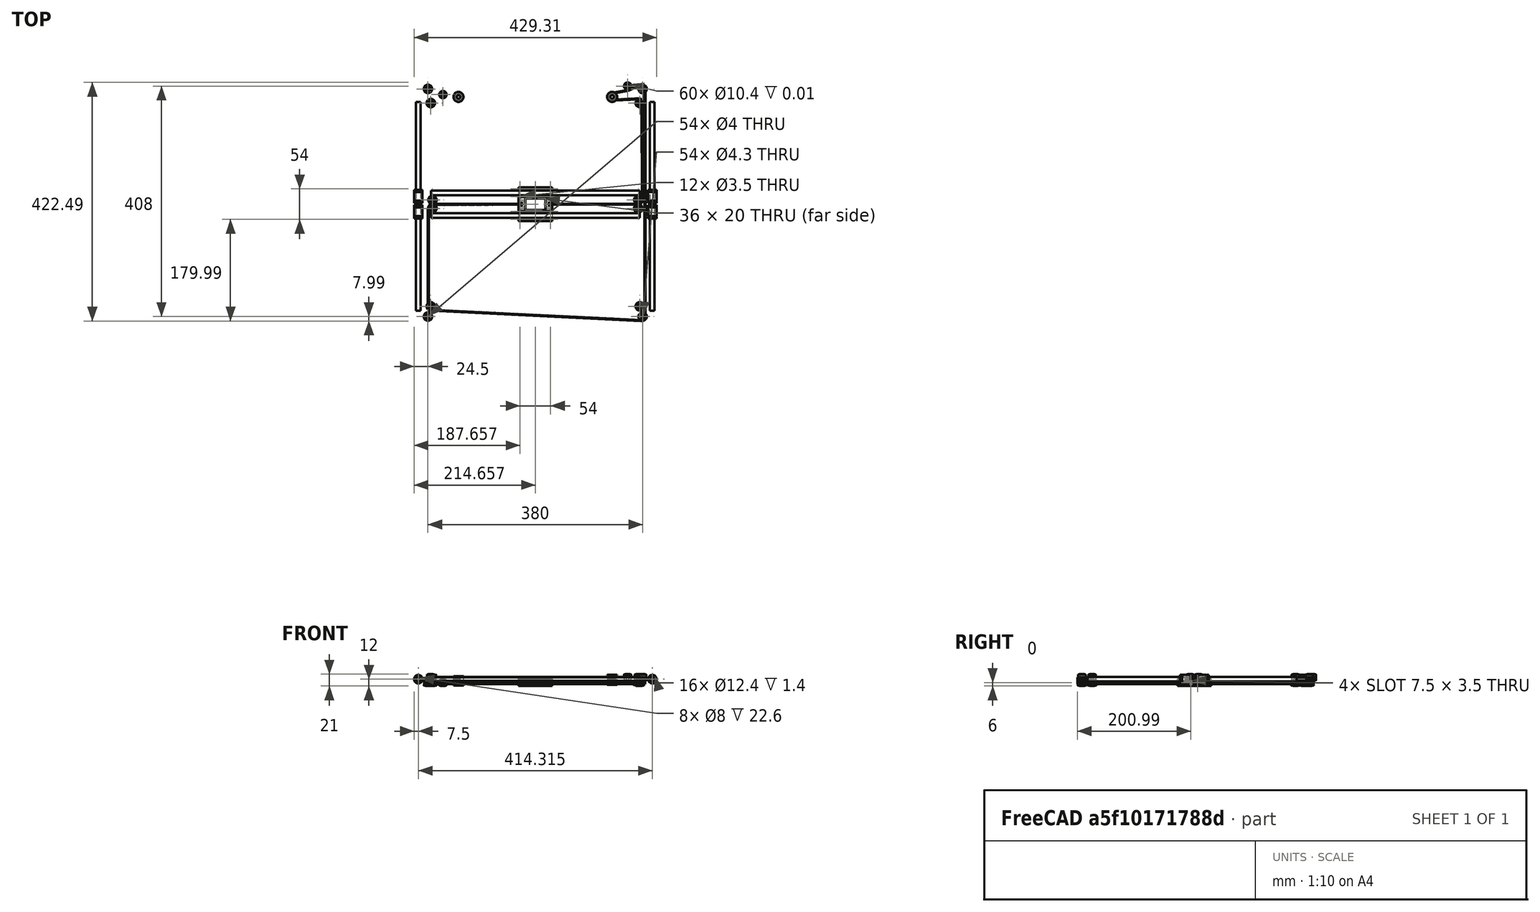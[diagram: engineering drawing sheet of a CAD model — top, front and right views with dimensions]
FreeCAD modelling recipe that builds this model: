
FCSTD DOCUMENT  (FreeCAD 0.16R4945 (Git))
Label: GT2-Belt_right
License: All rights reserved
LicenseURL: http://en.wikipedia.org/wiki/All_rights_reserved
objects: Part::Part2DObjectPython×17, Sketcher::SketchObject×5, Part::FeaturePython×3, App::DocumentObjectGroup×3, Part::Sweep×2, PartDesign::Pad×1, Part::Compound×1
note: 30 computed .brp shape members not serialized (recipe doc carries the construction recipe); baked Part::Feature solids carry a one-line shape summary decoded from their .brp

FEATURE [Part::FeaturePython] muxedAssembly  # WARN: FeaturePython — macro-defined, semantics opaque (R4)
  type = muxedAssembly
FEATURE [Sketcher::SketchObject] Sketch  label="Beltpath"
  ExternalGeometry = -> [muxedAssembly]
  Placement = pos=(0,0,13.243) rot=(0,0,1;0rad)
  Support = -> muxedAssembly [Face372]
  sketch-geometry (26):
    g0: LineSegment [constr] StartX=190.157 StartY=-169 StartZ=0 EndX=250.157 EndY=-169 EndZ=0
    g1: Circle [constr] CenterX=38 CenterY=-176.5 CenterZ=0 NormalX=0 NormalY=0 NormalZ=1 Radius=7.25
    g2: Circle [constr] CenterX=38 CenterY=-350 CenterZ=0 NormalX=0 NormalY=0 NormalZ=1 Radius=7.25
    g3: Circle [constr] CenterX=407 CenterY=-368 CenterZ=0 NormalX=0 NormalY=0 NormalZ=1 Radius=7.25
    g4: Circle [constr] CenterX=402.315 CenterY=-161.5 CenterZ=0 NormalX=0 NormalY=0 NormalZ=1 Radius=7.25
    g5: Circle [constr] CenterX=407 CenterY=35 CenterZ=0 NormalX=0 NormalY=0 NormalZ=1 Radius=7.25
    g6: Circle [constr] CenterX=402 CenterY=10 CenterZ=0 NormalX=0 NormalY=0 NormalZ=1 Radius=7.25
    g7: Circle [constr] CenterX=356 CenterY=21 CenterZ=0 NormalX=0 NormalY=0 NormalZ=1 Radius=6.04449
    g8: LineSegment StartX=250.157 StartY=-169 StartZ=0 EndX=402.327 EndY=-168.75 EndZ=0
    g9: ArcOfCircle CenterX=402.315 CenterY=-161.5 CenterZ=0 NormalX=0 NormalY=0 NormalZ=1 Radius=7.25 StartAngle=4.71403 EndAngle=6.28502
    g10: LineSegment StartX=409.565 StartY=-161.487 StartZ=0 EndX=409.25 EndY=10.0133 EndZ=0
    g11: ArcOfCircle CenterX=402 CenterY=10 CenterZ=0 NormalX=0 NormalY=0 NormalZ=1 Radius=7.25 StartAngle=0.00183673 EndAngle=1.621
    g12: LineSegment StartX=401.636 StartY=17.2409 StartZ=0 EndX=356.303 EndY=14.9631 EndZ=0
    g13: ArcOfCircle CenterX=356 CenterY=21 CenterZ=0 NormalX=0 NormalY=0 NormalZ=1 Radius=6.04449 StartAngle=1.76381 EndAngle=4.76259
    g14: ArcOfCircle CenterX=407 CenterY=35 CenterZ=0 NormalX=0 NormalY=0 NormalZ=1 Radius=7.26076 StartAngle=6.28316 EndAngle=8.24177
    g15: LineSegment StartX=414.261 StartY=34.9998 StartZ=0 EndX=414.25 EndY=-368 EndZ=0
    g16: ArcOfCircle CenterX=407 CenterY=-368 CenterZ=0 NormalX=0 NormalY=0 NormalZ=1 Radius=7.25 StartAngle=4.66365 EndAngle=6.28316
    g17: LineSegment StartX=406.647 StartY=-375.241 StartZ=0 EndX=37.6468 EndY=-357.241 EndZ=0
    g18: ArcOfCircle CenterX=38 CenterY=-350 CenterZ=0 NormalX=0 NormalY=0 NormalZ=1 Radius=7.25 StartAngle=3.14159 EndAngle=4.66365
    g19: LineSegment StartX=30.75 StartY=-350 StartZ=0 EndX=30.75 EndY=-176.5 EndZ=0
    g20: ArcOfCircle CenterX=38 CenterY=-176.5 CenterZ=0 NormalX=0 NormalY=0 NormalZ=1 Radius=7.25 StartAngle=1.57244 EndAngle=3.14159
    g21: LineSegment StartX=37.9881 StartY=-169.25 StartZ=0 EndX=190.157 EndY=-169 EndZ=0
    g22: Circle [constr] CenterX=383.517 CenterY=39.9241 CenterZ=0 NormalX=0 NormalY=0 NormalZ=1 Radius=7.25
    g23: LineSegment StartX=404.254 StartY=41.7216 StartZ=0 EndX=386.62 EndY=33.3716 EndZ=0
    g24: ArcOfCircle CenterX=383.517 CenterY=39.9241 CenterZ=0 NormalX=0 NormalY=0 NormalZ=1 Radius=7.25 StartAngle=4.9054 EndAngle=5.15462
    g25: LineSegment StartX=384.908 StartY=32.8088 StartZ=0 EndX=354.841 EndY=26.9323 EndZ=0
  constraints (67):
    c: PointOnObject(g0,g-6)
    c: PointOnObject(g0,g-7)
    c: Symmetric(g-6,g-6,g0)
    c: Coincident(g1,g-5)
    c: Coincident(g4,g-4)
    c: Coincident(g7,g-3)
    c: Radius(g7) = 6.04449
    c: Radius(g5) = 7.25
    c: Equal(g5,g6)
    c: Equal(g6,g4)
    c: Equal(g4,g1)
    c: Equal(g1,g2)
    c: Equal(g2,g3)
    c: Coincident(g0,g8)
    c: Tangent(g8,g9) = -1.5708
    c: Coincident(g9,g10)
    c: Tangent(g10,g11) = -1.5708
    c: Coincident(g11,g12)
    c: Tangent(g12,g13) = 1.5708
    c: Coincident(g14,g15)
    c: Tangent(g15,g16) = 1.5708
    c: Coincident(g16,g17)
    c: Tangent(g17,g18) = 1.5708
    c: Coincident(g18,g19)
    c: Tangent(g19,g20) = 1.5708
    c: Coincident(g20,g21)
    c: Coincident(g21,g0)
    c: Coincident(g4,g9)
    c: Coincident(g6,g11)
    c: Coincident(g7,g13)
    c: Coincident(g5,g14)
    c: Coincident(g3,g16)
    c: Coincident(g18,g2)
    c: Coincident(g1,g20)
    c: PointOnObject(g8,g4)
    c: Tangent(g9,g10) = -1.5708
    c: PointOnObject(g10,g6)
    c: Tangent(g11,g12) = -1.5708
    c: PointOnObject(g12,g7)
    c: Tangent(g14,g15) = 1.5708
    c: PointOnObject(g15,g3)
    c: Tangent(g16,g17) = 1.5708
    c: PointOnObject(g17,g2)
    c: Tangent(g18,g19) = 1.5708
    c: PointOnObject(g19,g1)
    c: Tangent(g20,g21) = 1.5708
    c: Equal(g22,g5)
    c: Coincident(g14,g23)
    c: Tangent(g23,g5)
    c: Tangent(g23,g24) = 1.5708
    c: Coincident(g24,g25)
    c: Coincident(g25,g13)
    c: Tangent(g25,g7)
    c: PointOnObject(g23,g22)
    c: DistanceX(g22) = 383.517
    c: DistanceY(g22) = 39.9241
    c: PointOnObject(g24,g22)
    c: Tangent(g24,g25) = 1.5708
    c: Coincident(g22,g24)
    c: DistanceY(g-11,g2) = 0
    c: DistanceX(g-11,g2) = 3
    c: DistanceY(g3,g-10) = 0
    c: DistanceX(g-10,g3) = -3
    c: DistanceY(g6,g-8) = 0
    c: DistanceX(g6,g-8) = 3
    c: DistanceY(g5,g-9) = 0
    c: DistanceX(g5,g-9) = 3
FEATURE [Sketcher::SketchObject] Sketch001
  Placement = pos=(250.157,0,0) rot=(0.57735,0.57735,0.57735;2.0944rad)
  Support = -> muxedAssembly [Face737]
  sketch-geometry (4):
    g0: LineSegment StartX=-169.757 StartY=13.2439 StartZ=0 EndX=-168.257 EndY=13.2439 EndZ=0
    g1: LineSegment StartX=-168.257 StartY=13.2439 StartZ=0 EndX=-168.257 EndY=19.2439 EndZ=0
    g2: LineSegment StartX=-168.257 StartY=19.2439 StartZ=0 EndX=-169.757 EndY=19.2439 EndZ=0
    g3: LineSegment StartX=-169.757 StartY=19.2439 StartZ=0 EndX=-169.757 EndY=13.2439 EndZ=0
  constraints (10):
    c: Coincident(g0,g1)
    c: Coincident(g1,g2)
    c: Coincident(g2,g3)
    c: Coincident(g3,g0)
    c: Horizontal(g0)
    c: Horizontal(g2)
    c: Vertical(g1)
    c: Vertical(g3)
    c: Distance(g2) = 1.5
    c: Distance(g1) = 6
FEATURE [Part::FeaturePython] Bearings_import01  # a2plus imported part (geometry in sourceFile) (typed FeaturePython)
  fixedPosition = true
  sourceFile = <userpath>/CloudStation/Hobbyprojekte/3D Drucker/CoreXY/Freecad/Assembly/XY/Bearings.FCStd
  timeLastImport = 1431280628
FEATURE [Part::Sweep] Sweep  label="Sweep (GT2-Belt simple)"
  Frenet = false
  Sections = -> [Sketch001]
  Solid = true
  Spine = -> Sketch [Edge1,Edge2,Edge3,Edge4,Edge5,Edge6,Edge7,Edge8,Edge9,Edge10,Edge11,Edge12,Edge13,Edge14,Edge15,Edge16,Edge17]
  Transition = 1
FEATURE [Sketcher::SketchObject] Sketch002  label="Timing Belt Master Sketch"
  Placement = pos=(0,0,0) rot=(1,0,0;1.5708rad)
  sketch-geometry (11):
    g0: Circle CenterX=0 CenterY=-0.449 CenterZ=0 NormalX=0 NormalY=0 NormalZ=1 Radius=0.555
    g1: LineSegment [constr] StartX=-1 StartY=-1.004 StartZ=0 EndX=1 EndY=-1.004 EndZ=0
    g2: LineSegment StartX=-1 StartY=-0.254 StartZ=0 EndX=1 EndY=-0.254 EndZ=0
    g3: LineSegment StartX=-1 StartY=0.376 StartZ=0 EndX=1 EndY=0.376 EndZ=0
    g4: LineSegment StartX=-1 StartY=0.376 StartZ=0 EndX=-1 EndY=-1.004 EndZ=0
    g5: LineSegment StartX=1 StartY=0.376 StartZ=0 EndX=1 EndY=-1.004 EndZ=0
    g6: LineSegment [constr] StartX=-1 StartY=-0.449 StartZ=0 EndX=1 EndY=-0.449 EndZ=0
    g7: Circle CenterX=-0.740175 CenterY=-0.404 CenterZ=0 NormalX=0 NormalY=0 NormalZ=1 Radius=0.15
    g8: Circle CenterX=0.740175 CenterY=-0.404 CenterZ=0 NormalX=0 NormalY=0 NormalZ=1 Radius=0.15
    g9: Circle CenterX=-0.4 CenterY=-0.254 CenterZ=0 NormalX=0 NormalY=0 NormalZ=1 Radius=1
    g10: Circle CenterX=0.4 CenterY=-0.254 CenterZ=0 NormalX=0 NormalY=0 NormalZ=1 Radius=1
  constraints (33):
    c: Radius(g0) = 0.555
    c: PointOnObject(g0,g-2)
    c: Horizontal(g1)
    c: Tangent(g1,g0)
    c: DistanceX(g1) = 2
    c: Symmetric(g1,g1,g-2)
    c: Horizontal(g2)
    c: DistanceY(g2,g1) = -0.75
    c: Horizontal(g3)
    c: Equal(g1,g2)
    c: Equal(g2,g3)
    c: Vertical(g4)
    c: Coincident(g4,g1)
    c: Coincident(g4,g3)
    c: PointOnObject(g2,g4)
    c: Coincident(g5,g1)
    c: Coincident(g5,g3)
    c: DistanceY(g3,g1) = -1.38
    c: PointOnObject(g0,g6)
    c: DistanceY(g-1,g2) = -0.254
    c: Horizontal(g6)
    c: PointOnObject(g6,g4)
    c: PointOnObject(g6,g5)
    c: Radius(g7) = 0.15
    c: Equal(g8,g7)
    c: Symmetric(g7,g8,g-2)
    c: Radius(g9) = 1
    c: Equal(g10,g9)
    c: Symmetric(g10,g9,g-2)
    c: DistanceX(g-1,g10) = 0.4
    c: DistanceY(g7,g3) = 0.78
    c: DistanceX(g7,g3) = -0.259825
    c: PointOnObject(g10,g2)
FEATURE [App::DocumentObjectGroup] Group  label="Master Sketch"
  Group = -> [Sketch002]
FEATURE [Part::Part2DObjectPython] Circle  # Draft 2D object (typed FeaturePython)
  FirstAngle = 0
  LastAngle = 0
  MakeFace = true
  Placement = pos=(0,-0.449,0) rot=(0,0,1;0rad)
  Radius = 0.555
FEATURE [Part::Part2DObjectPython] Line  # Draft 2D object (typed FeaturePython)
  ChamferSize = 0
  Closed = false
  End = (1,-0.254,0)
  FilletRadius = 0
  MakeFace = true
  Points = (2) [(-1,-0.254,0),(1,-0.254,0)]
  Start = (-1,-0.254,0)
FEATURE [Part::Part2DObjectPython] DWire  # Draft 2D object (typed FeaturePython)
  ChamferSize = 0
  Closed = false
  End = (1,-1.004,0)
  FilletRadius = 0
  MakeFace = true
  Points = (4) [(-1,-1.004,0),(-1,0.376,0),(1,0.376,0),(1,-1.004,0)]
  Start = (-1,-1.004,0)
FEATURE [Part::Part2DObjectPython] Circle001  # Draft 2D object (typed FeaturePython)
  FirstAngle = 0
  LastAngle = 0
  MakeFace = true
  Placement = pos=(-0.740175,-0.404,0) rot=(0,0,1;0rad)
  Radius = 0.15
FEATURE [Part::Part2DObjectPython] Circle002  # Draft 2D object (typed FeaturePython)
  FirstAngle = 0
  LastAngle = 0
  MakeFace = true
  Placement = pos=(0.740175,-0.404,0) rot=(0,0,1;0rad)
  Radius = 0.15
FEATURE [Part::Part2DObjectPython] Circle003  # Draft 2D object (typed FeaturePython)
  FirstAngle = 0
  LastAngle = 0
  MakeFace = true
  Placement = pos=(-0.4,-0.254,0) rot=(0,0,1;0rad)
  Radius = 1
FEATURE [Part::Part2DObjectPython] Circle004  # Draft 2D object (typed FeaturePython)
  FirstAngle = 0
  LastAngle = 0
  MakeFace = true
  Placement = pos=(0.4,-0.254,0) rot=(0,0,1;0rad)
  Radius = 1
FEATURE [App::DocumentObjectGroup] Group001  label="Draft from Sketch"
  Group = -> [Circle,Line,DWire,Circle001,Circle002,Circle003,Circle004]
FEATURE [Part::Part2DObjectPython] Arc  # Draft 2D object (typed FeaturePython)
  FirstAngle = 7.49472
  LastAngle = 90
  MakeFace = false
  Placement = pos=(-0.740175,-0.404,0) rot=(0,0,1;0rad)
  Radius = 0.15
FEATURE [Part::Part2DObjectPython] Arc001  # Draft 2D object (typed FeaturePython)
  FirstAngle = 90
  LastAngle = 172.505
  MakeFace = false
  Placement = pos=(0.740175,-0.404,0) rot=(0,0,1;0rad)
  Radius = 0.15
FEATURE [Part::Part2DObjectPython] Line001  # Draft 2D object (typed FeaturePython)
  ChamferSize = 0
  Closed = false
  End = (-1,-0.254,0)
  FilletRadius = 0
  MakeFace = false
  Points = (2) [(-0.740175,-0.254,0),(-1,-0.254,0)]
  Start = (-0.740175,-0.254,0)
FEATURE [Part::Part2DObjectPython] Line002  # Draft 2D object (typed FeaturePython)
  ChamferSize = 0
  Closed = false
  End = (1,-0.254,0)
  FilletRadius = 0
  MakeFace = false
  Points = (2) [(0.740175,-0.254,0),(1,-0.254,0)]
  Start = (0.740175,-0.254,0)
FEATURE [Part::Part2DObjectPython] Arc002  # Draft 2D object (typed FeaturePython)
  FirstAngle = -154.011
  LastAngle = -25.9892
  MakeFace = false
  Placement = pos=(0,-0.449,0) rot=(0,0,1;0rad)
  Radius = 0.555
FEATURE [Part::Part2DObjectPython] Arc003  # Draft 2D object (typed FeaturePython)
  FirstAngle = -25.9892
  LastAngle = -7.49472
  MakeFace = false
  Placement = pos=(-0.4,-0.254,0) rot=(0,0,1;0rad)
  Radius = 1
FEATURE [Part::Part2DObjectPython] Arc004  # Draft 2D object (typed FeaturePython)
  FirstAngle = -172.505
  LastAngle = -154.011
  MakeFace = false
  Placement = pos=(0.4,-0.254,0) rot=(0,0,1;0rad)
  Radius = 1
FEATURE [Part::Part2DObjectPython] Line003  # Draft 2D object (typed FeaturePython)
  ChamferSize = 0
  Closed = false
  End = (-1,0.376,0)
  FilletRadius = 0
  MakeFace = false
  Points = (2) [(-1,-0.254,0),(-1,0.376,0)]
  Start = (-1,-0.254,0)
FEATURE [Part::Part2DObjectPython] Line004  # Draft 2D object (typed FeaturePython)
  ChamferSize = 0
  Closed = false
  End = (1,0.376,0)
  FilletRadius = 0
  MakeFace = false
  Points = (2) [(1,-0.254,0),(1,0.376,0)]
  Start = (1,-0.254,0)
FEATURE [Part::Part2DObjectPython] Line005  # Draft 2D object (typed FeaturePython)
  ChamferSize = 0
  Closed = false
  End = (1,0.376,0)
  FilletRadius = 0
  MakeFace = false
  Points = (2) [(-1,0.376,0),(1,0.376,0)]
  Start = (-1,0.376,0)
FEATURE [App::DocumentObjectGroup] Group002  label="Outline from Draft"
  Group = -> [Arc,Arc001,Line001,Line002,Arc002,Arc003,Arc004,Line003,Line004,Line005]
FEATURE [Sketcher::SketchObject] Sketch003  label="Timing Belt sketch from outline"
  Placement = pos=(0,0,0) rot=(0,-0.707107,0.707107;3.14159rad)
  sketch-geometry (10):
    g0: ArcOfCircle CenterX=-0.740173 CenterY=-0.403997 CenterZ=0 NormalX=0 NormalY=0 NormalZ=1 Radius=0.149997 StartAngle=0.134719 EndAngle=1.57082
    g1: LineSegment StartX=1 StartY=-0.254 StartZ=0 EndX=1 EndY=0.376 EndZ=0
    g2: ArcOfCircle CenterX=0.740176 CenterY=-0.404 CenterZ=0 NormalX=0 NormalY=0 NormalZ=1 Radius=0.15 StartAngle=1.5708 EndAngle=3.01411
    g3: LineSegment StartX=0.740176 StartY=-0.254 StartZ=0 EndX=1 EndY=-0.254 EndZ=0
    g4: LineSegment StartX=-0.740176 StartY=-0.254 StartZ=0 EndX=-1 EndY=-0.254 EndZ=0
    g5: ArcOfCircle CenterX=0 CenterY=-0.448894 CenterZ=0 NormalX=0 NormalY=0 NormalZ=1 Radius=0.555048 StartAngle=3.59519 EndAngle=5.83002
    g6: ArcOfCircle CenterX=-0.400001 CenterY=-0.254 CenterZ=0 NormalX=0 NormalY=0 NormalZ=1 Radius=1 StartAngle=5.82992 EndAngle=6.15188
    g7: LineSegment StartX=-1 StartY=0.376 StartZ=0 EndX=1 EndY=0.376 EndZ=0
    g8: ArcOfCircle CenterX=0.400001 CenterY=-0.254 CenterZ=0 NormalX=0 NormalY=0 NormalZ=1 Radius=1 StartAngle=3.27181 EndAngle=3.5951
    g9: LineSegment StartX=-1 StartY=-0.254 StartZ=0 EndX=-1 EndY=0.376 EndZ=0
  constraints (34):
    c: Coincident(g7,g9)
    c: Coincident(g1,g7)
    c: Coincident(g4,g9)
    c: Coincident(g0,g4)
    c: Coincident(g0,g8)
    c: Coincident(g5,g8)
    c: Coincident(g5,g6)
    c: Coincident(g2,g6)
    c: Coincident(g2,g3)
    c: Coincident(g1,g3)
    c: PointOnObject(g5,g-2)
    c: DistanceX(g7) = 2
    c: Symmetric(g7,g1,g-2)
    c: Equal(g9,g1)
    c: Equal(g4,g3)
    c: DistanceY(g9) = 0.63
    c: DistanceX(g4) = -0.259824
    c: Vertical(g9)
    c: Horizontal(g4)
    c: Horizontal(g3)
    c: Symmetric(g1,g4,g-2)
    c: DistanceY(g-1,g7) = 0.376
    c: DistanceX(g8) = 0.400001
    c: DistanceY(g8) = -0.254
    c: DistanceX(g6) = -0.400001
    c: DistanceY(g6) = -0.254
    c: DistanceX(g0) = -0.740173
    c: DistanceY(g0) = -0.403997
    c: DistanceX(g2) = 0.740176
    c: DistanceY(g2) = -0.404
    c: Equal(g8,g6)
    c: Radius(g5) = 0.555048
    c: DistanceX(g5) = 0.499025
    c: DistanceY(g5) = -0.691901
FEATURE [PartDesign::Pad] Pad  label="Timing Belt GT2"
  Length = 6
  Length2 = 100
  Placement = pos=(0,0,0) rot=(0,-0.707107,0.707107;3.14159rad)
  Sketch = -> Sketch003
  Type = 0
FEATURE [Sketcher::SketchObject] Sketch004  label="Belt-Back"
  Placement = pos=(190.157,-169,13.243) rot=(0.57735,0.57735,0.57735;2.0944rad)
  sketch-geometry (4):
    g0: LineSegment StartX=0.266 StartY=0 StartZ=0 EndX=0.486 EndY=0 EndZ=0
    g1: LineSegment StartX=0.486 StartY=0 StartZ=0 EndX=0.486 EndY=-6 EndZ=0
    g2: LineSegment StartX=0.486 StartY=-6 StartZ=0 EndX=0.266 EndY=-6 EndZ=0
    g3: LineSegment StartX=0.266 StartY=-6 StartZ=0 EndX=0.266 EndY=0 EndZ=0
  constraints (12):
    c: Coincident(g0,g1)
    c: Coincident(g1,g2)
    c: Coincident(g2,g3)
    c: Coincident(g3,g0)
    c: Horizontal(g0)
    c: Horizontal(g2)
    c: Vertical(g1)
    c: Vertical(g3)
    c: Distance(g1) = 6
    c: Distance(g0) = 0.22
    c: DistanceY(g-1,g0) = 0
    c: DistanceX(g-1,g0) = 0.266
FEATURE [Part::FeaturePython] PathArray  # WARN: FeaturePython — macro-defined, semantics opaque (R4)
  Align = true
  Base = -> Pad
  Count = 806
  PathObj = -> Sketch
  Xlate = (0,0,0)
FEATURE [Part::Sweep] Sweep001
  Frenet = false
  Sections = -> [Sketch004]
  Solid = false
  Spine = -> Sketch [Edge17,Edge16,Edge15,Edge14,Edge13,Edge12,Edge11,Edge10,Edge9,Edge8,Edge7,Edge6,Edge5,Edge4,Edge3,Edge2,Edge1]
  Transition = 1
FEATURE [Part::Compound] Compound
  Links = -> [PathArray,Sweep001]
